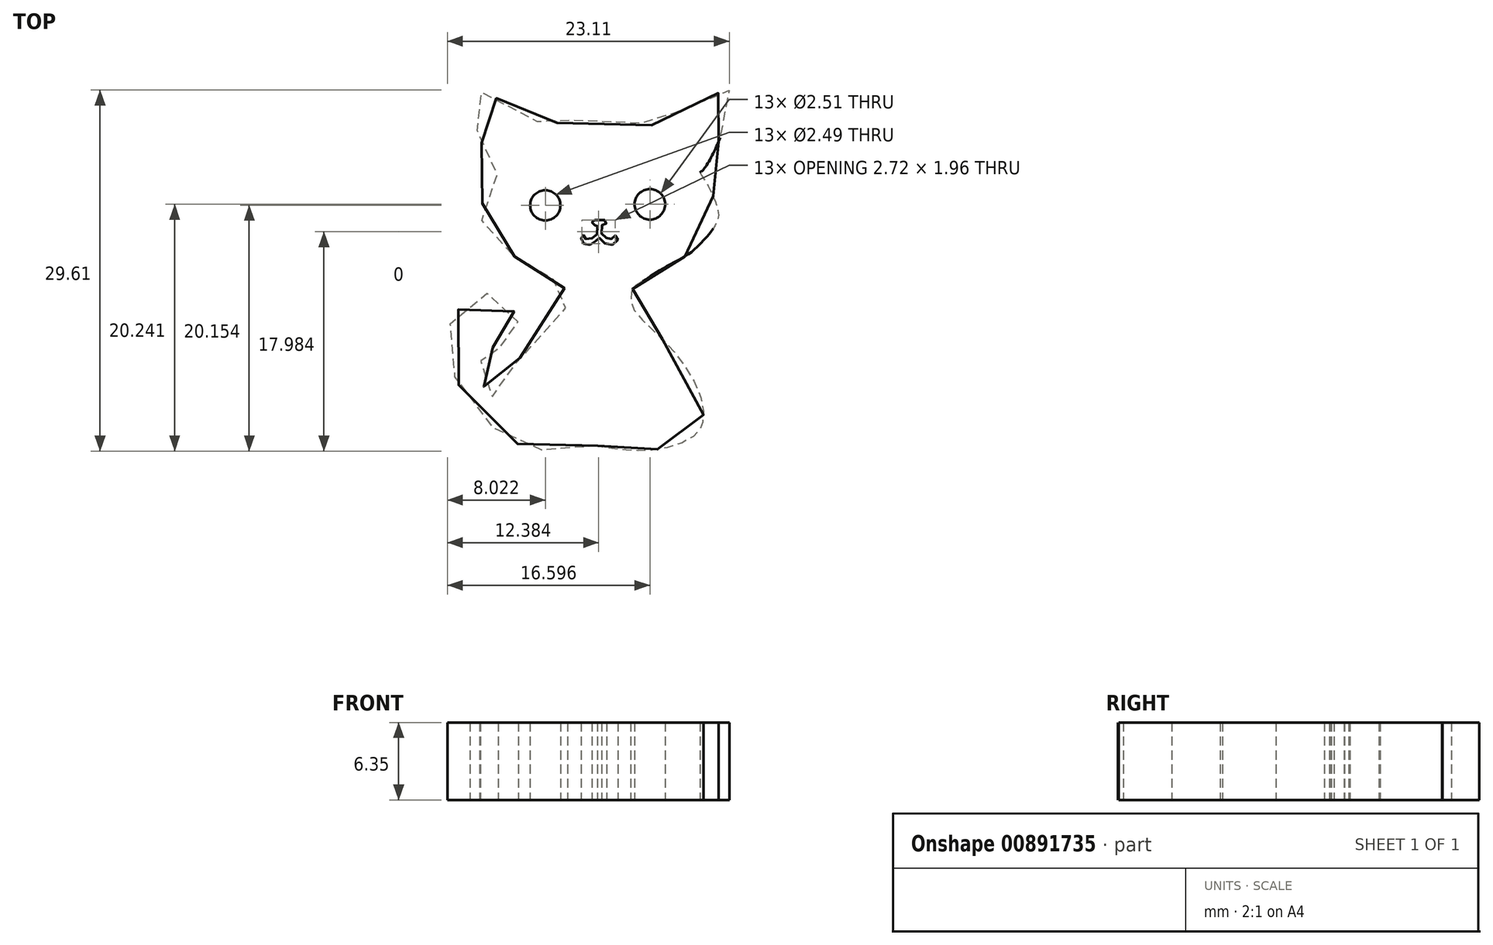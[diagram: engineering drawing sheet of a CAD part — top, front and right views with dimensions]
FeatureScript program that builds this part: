
annotation { "Feature Type Name" : "Feature", "Feature Type Description" : "" }
export const myFeature = defineFeature(function(context is Context, id is Id, definition is map)
    precondition{}
    {
        {
            var Q0;
            Q0=qCreatedBy(makeId("Top.planeOp"),FACE);
            var sketch = newSketch(context, id + "F0", { "sketchPlane" : qUnion([Q0])});
            skPoint(sketch, "E0.middle", {"position": v(0, 0) * mm});
            skPoint(sketch, "E0.bottom.start.orphan", {"position": v(12.73, -13.78) * mm});
            skCircle(sketch, "E1", {"center": v(-3.47, 3) * mm, "radius": 1.24 * mm});
            skCircle(sketch, "E2", {"center": v(5.1, 3.1) * mm, "radius": 1.25 * mm});
            skFitSpline(sketch, "E3", {"points": [v(0.6, 1.81) * mm, v(1.33, 1.81) * mm, v(1.52, 1.72) * mm, v(1.55, 1.57) * mm, v(1.43, 1.41) * mm, v(1.2, 1.38) * mm, v(1.18, 1.38) * mm, v(1.15, 0.7) * mm, v(1.15, 0.67) * mm, v(1.27, 0.55) * mm, v(1.64, 0.27) * mm, v(1.86, 0.2) * mm, v(2.01, 0.3) * mm, v(2.14, 0.45) * mm, v(2.3, 0.55) * mm, v(2.45, 0.45) * mm, v(2.42, 0) * mm, v(2.01, -0.23) * mm, v(1.64, -0.2) * mm, v(1.09, 0.14) * mm, v(0.96, 0.33) * mm, v(0.87, 0.33) * mm, v(0.75, 0.17) * mm, v(0.44, -0.13) * mm, v(0.13, -0.23) * mm, v(-0.15, -0.2) * mm, v(-0.46, 0) * mm, v(-0.52, 0.2) * mm, v(-0.52, 0.52) * mm, v(-0.43, 0.55) * mm, v(-0.3, 0.55) * mm, v(-0.21, 0.42) * mm, v(-0.15, 0.24) * mm, v(0.13, 0.17) * mm, v(0.56, 0.45) * mm, v(0.75, 0.6) * mm, v(0.8, 0.73) * mm, v(0.8, 1.35) * mm, v(0.8, 1.4) * mm, v(0.73, 1.4) * mm, v(0.54, 1.4) * mm, v(0.45, 1.45) * mm, v(0.38, 1.56) * mm, v(0.4, 1.72) * mm, v(0.47, 1.8) * mm, v(0.6, 1.81) * mm]});
            skFitSpline(sketch, "E4", {"points": [v(0.84, -16.71) * mm, v(-0.5, -17.03) * mm, v(-3.94, -17.03) * mm, v(-6.18, -16.35) * mm, v(-7.9, -15.1) * mm, v(-9.77, -13.18) * mm, v(-11.38, -9.38) * mm, v(-11.42, -7.48) * mm, v(-10.94, -6.04) * mm, v(-9.26, -4.4) * mm, v(-7.85, -4.27) * mm, v(-6.61, -4.91) * mm, v(-5.73, -6.48) * mm, v(-5.85, -7.76) * mm, v(-6.53, -8.64) * mm, v(-7.5, -8.76) * mm, v(-7.94, -8.6) * mm, v(-8.38, -8.64) * mm, v(-8.62, -9.12) * mm, v(-8.82, -10.14) * mm, v(-8.73, -11.36) * mm, v(-8.03, -12.5) * mm, v(-7.6, -12.76) * mm, v(-7.44, -12.7) * mm, v(-7.24, -12.25) * mm, v(-5.13, -8.97) * mm, v(-1.96, -5.64) * mm, v(-1.65, -4.81) * mm, v(-2.06, -3.51) * mm, v(-2.53, -3.25) * mm, v(-3.41, -2.63) * mm, v(-5.23, -1.64) * mm, v(-6.54, -0.8) * mm, v(-7.93, 0.45) * mm, v(-8.74, 2) * mm, v(-8.54, 3.42) * mm, v(-7.4, 5.58) * mm, v(-7.32, 5.64) * mm, v(-7.4, 5.91) * mm, v(-8.54, 7.8) * mm, v(-9.62, 12.32) * mm, v(-9.35, 12.46) * mm, v(-8.6, 12.25) * mm, v(-5.84, 10.97) * mm, v(-3.75, 9.56) * mm, v(-3.61, 9.42) * mm, v(-3.28, 9.56) * mm, v(-1.05, 10.03) * mm, v(2.45, 10.1) * mm, v(5.5, 9.49) * mm, v(5.7, 9.43) * mm, v(5.85, 9.58) * mm, v(8.08, 11.1) * mm, v(11.26, 12.4) * mm, v(11.57, 12.45) * mm, v(11.62, 12.24) * mm, v(11.47, 10.89) * mm, v(10.58, 7.87) * mm, v(9.33, 5.79) * mm, v(9.23, 5.74) * mm, v(9.28, 5.58) * mm, v(9.8, 4.75) * mm, v(10.63, 2.82) * mm, v(10.58, 1.63) * mm, v(8.76, -0.61) * mm, v(7.4, -1.5) * mm, v(5.52, -2.57) * mm, v(4.37, -3.31) * mm, v(3.77, -3.72) * mm, v(3.56, -4.33) * mm, v(3.63, -5.2) * mm, v(4.58, -6.49) * mm, v(6.26, -8.1) * mm, v(8.22, -10.53) * mm, v(9.43, -13.37) * mm, v(9.43, -14.78) * mm, v(9.22, -15.34) * mm, v(8.33, -16.17) * mm, v(6.1, -16.95) * mm, v(3.91, -17.1) * mm, v(2.45, -17) * mm, v(1.3, -16.84) * mm, v(0.84, -16.71) * mm]});
            skSolve(sketch);
        }
        {
            var Q0;
            Q0 = qSketchRegion(id + "F0", true);
            extrude(context, id + "F1", {"entities" : qUnion([Q0]), "depth" : 6.35 * mm, "offsetDistance" : 25.4 * mm});
        }
    });
